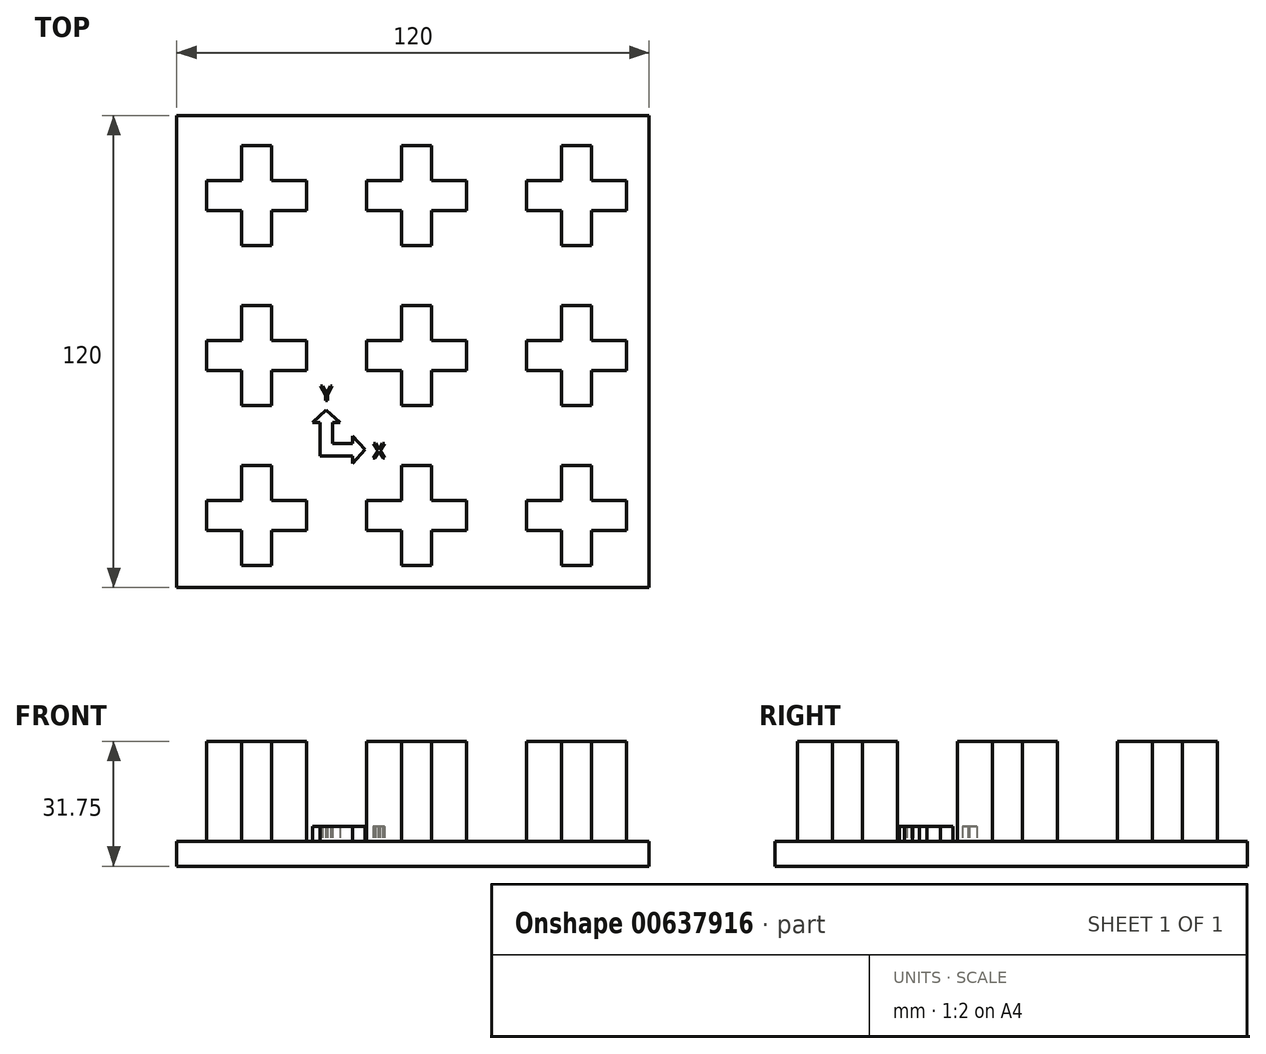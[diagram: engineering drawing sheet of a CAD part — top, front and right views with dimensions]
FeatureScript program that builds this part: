
annotation { "Feature Type Name" : "Feature", "Feature Type Description" : "" }
export const myFeature = defineFeature(function(context is Context, id is Id, definition is map)
    precondition{}
    {
        {
            var Q0;
            Q0=qCreatedBy(makeId("Top.planeOp"),FACE);
            var sketch = newSketch(context, id + "F0", { "sketchPlane" : qUnion([Q0])});
            skLineSegment(sketch, "E0.bottom", {"start": v(62.34, 71.9) * mm, "end": v(-57.66, 71.9) * mm});
            skLineSegment(sketch, "E0.top", {"start": v(62.34, -48.1) * mm, "end": v(-57.66, -48.1) * mm});
            skLineSegment(sketch, "E0.left", {"start": v(62.34, 71.9) * mm, "end": v(62.34, -48.1) * mm});
            skLineSegment(sketch, "E0.right", {"start": v(-57.66, 71.9) * mm, "end": v(-57.66, -48.1) * mm});
            skSolve(sketch);
        }
        {
            var Q0;
            Q0 = qSketchRegion(id + "F0", true);
            extrude(context, id + "F1", {"entities" : qUnion([Q0]), "depth" : 6.35 * mm, "offsetDistance" : 25.4 * mm});
        }
        {
            var Q0;
            Q0=makeQuery(id+"F1.opExtrude","CAP_FACE",FACE,{"disambiguationData":[OSD([sQuery(id+"F0.wireOp",EDGE,"E0.bottom"),sQuery(id+"F0.wireOp",EDGE,"E0.top"),sQuery(id+"F0.wireOp",EDGE,"E0.left"),sQuery(id+"F0.wireOp",EDGE,"E0.right")])],"isStart":false});
            var sketch = newSketch(context, id + "F2", { "sketchPlane" : qUnion([Q0])});
            skLineSegment(sketch, "E1.bottom", {"start": v(-41.15, 64.28) * mm, "end": v(-33.53, 64.28) * mm});
            skLineSegment(sketch, "E1.top", {"start": v(-41.15, 38.88) * mm, "end": v(-33.53, 38.88) * mm});
            skLineSegment(sketch, "E1.left", {"start": v(-41.15, 64.28) * mm, "end": v(-41.15, 38.88) * mm});
            skLineSegment(sketch, "E1.right", {"start": v(-33.53, 64.28) * mm, "end": v(-33.53, 38.88) * mm});
            skLineSegment(sketch, "E2.bottom", {"start": v(-50.04, 55.4) * mm, "end": v(-24.64, 55.4) * mm});
            skLineSegment(sketch, "E2.top", {"start": v(-50.04, 47.77) * mm, "end": v(-24.64, 47.77) * mm});
            skLineSegment(sketch, "E2.left", {"start": v(-50.04, 55.4) * mm, "end": v(-50.04, 47.77) * mm});
            skLineSegment(sketch, "E2.right", {"start": v(-24.64, 55.4) * mm, "end": v(-24.64, 47.77) * mm});
            skLineSegment(sketch, "E3.0.1.0", {"start": v(-24.64, 14.75) * mm, "end": v(-24.64, 7.13) * mm});
            skLineSegment(sketch, "E3.0.1.1", {"start": v(-41.15, 23.64) * mm, "end": v(-33.53, 23.64) * mm});
            skLineSegment(sketch, "E3.0.1.2", {"start": v(-41.15, -1.76) * mm, "end": v(-33.53, -1.76) * mm});
            skLineSegment(sketch, "E3.0.1.3", {"start": v(-41.15, 23.64) * mm, "end": v(-41.15, -1.76) * mm});
            skLineSegment(sketch, "E3.0.1.4", {"start": v(-33.53, 23.64) * mm, "end": v(-33.53, -1.76) * mm});
            skLineSegment(sketch, "E3.0.1.5", {"start": v(-50.04, 14.75) * mm, "end": v(-24.64, 14.75) * mm});
            skLineSegment(sketch, "E3.0.1.6", {"start": v(-50.04, 7.13) * mm, "end": v(-24.64, 7.13) * mm});
            skLineSegment(sketch, "E3.0.1.7", {"start": v(-50.04, 14.75) * mm, "end": v(-50.04, 7.13) * mm});
            skLineSegment(sketch, "E3.0.2.0", {"start": v(-24.64, -25.89) * mm, "end": v(-24.64, -33.5) * mm});
            skLineSegment(sketch, "E3.0.2.1", {"start": v(-41.15, -17) * mm, "end": v(-33.53, -17) * mm});
            skLineSegment(sketch, "E3.0.2.2", {"start": v(-41.15, -42.4) * mm, "end": v(-33.53, -42.4) * mm});
            skLineSegment(sketch, "E3.0.2.3", {"start": v(-41.15, -17) * mm, "end": v(-41.15, -42.4) * mm});
            skLineSegment(sketch, "E3.0.2.4", {"start": v(-33.53, -17) * mm, "end": v(-33.53, -42.4) * mm});
            skLineSegment(sketch, "E3.0.2.5", {"start": v(-50.04, -25.89) * mm, "end": v(-24.64, -25.89) * mm});
            skLineSegment(sketch, "E3.0.2.6", {"start": v(-50.04, -33.5) * mm, "end": v(-24.64, -33.5) * mm});
            skLineSegment(sketch, "E3.0.2.7", {"start": v(-50.04, -25.89) * mm, "end": v(-50.04, -33.5) * mm});
            skLineSegment(sketch, "E3.1.0.0", {"start": v(16, 55.4) * mm, "end": v(16, 47.77) * mm});
            skLineSegment(sketch, "E3.1.0.1", {"start": v(-0.5, 64.28) * mm, "end": v(7.11, 64.28) * mm});
            skLineSegment(sketch, "E3.1.0.2", {"start": v(-0.5, 38.88) * mm, "end": v(7.11, 38.88) * mm});
            skLineSegment(sketch, "E3.1.0.3", {"start": v(-0.5, 64.28) * mm, "end": v(-0.5, 38.88) * mm});
            skLineSegment(sketch, "E3.1.0.4", {"start": v(7.11, 64.28) * mm, "end": v(7.11, 38.88) * mm});
            skLineSegment(sketch, "E3.1.0.5", {"start": v(-9.4, 55.4) * mm, "end": v(16, 55.4) * mm});
            skLineSegment(sketch, "E3.1.0.6", {"start": v(-9.4, 47.77) * mm, "end": v(16, 47.77) * mm});
            skLineSegment(sketch, "E3.1.0.7", {"start": v(-9.4, 55.4) * mm, "end": v(-9.4, 47.77) * mm});
            skLineSegment(sketch, "E3.1.1.0", {"start": v(16, 14.75) * mm, "end": v(16, 7.13) * mm});
            skLineSegment(sketch, "E3.1.1.1", {"start": v(-0.5, 23.64) * mm, "end": v(7.11, 23.64) * mm});
            skLineSegment(sketch, "E3.1.1.2", {"start": v(-0.5, -1.76) * mm, "end": v(7.11, -1.76) * mm});
            skLineSegment(sketch, "E3.1.1.3", {"start": v(-0.5, 23.64) * mm, "end": v(-0.5, -1.76) * mm});
            skLineSegment(sketch, "E3.1.1.4", {"start": v(7.11, 23.64) * mm, "end": v(7.11, -1.76) * mm});
            skLineSegment(sketch, "E3.1.1.5", {"start": v(-9.4, 14.75) * mm, "end": v(16, 14.75) * mm});
            skLineSegment(sketch, "E3.1.1.6", {"start": v(-9.4, 7.13) * mm, "end": v(16, 7.13) * mm});
            skLineSegment(sketch, "E3.1.1.7", {"start": v(-9.4, 14.75) * mm, "end": v(-9.4, 7.13) * mm});
            skLineSegment(sketch, "E3.1.2.0", {"start": v(16, -25.89) * mm, "end": v(16, -33.5) * mm});
            skLineSegment(sketch, "E3.1.2.1", {"start": v(-0.5, -17) * mm, "end": v(7.11, -17) * mm});
            skLineSegment(sketch, "E3.1.2.2", {"start": v(-0.5, -42.4) * mm, "end": v(7.11, -42.4) * mm});
            skLineSegment(sketch, "E3.1.2.3", {"start": v(-0.5, -17) * mm, "end": v(-0.5, -42.4) * mm});
            skLineSegment(sketch, "E3.1.2.4", {"start": v(7.11, -17) * mm, "end": v(7.11, -42.4) * mm});
            skLineSegment(sketch, "E3.1.2.5", {"start": v(-9.4, -25.89) * mm, "end": v(16, -25.89) * mm});
            skLineSegment(sketch, "E3.1.2.6", {"start": v(-9.4, -33.5) * mm, "end": v(16, -33.5) * mm});
            skLineSegment(sketch, "E3.1.2.7", {"start": v(-9.4, -25.89) * mm, "end": v(-9.4, -33.5) * mm});
            skLineSegment(sketch, "E3.2.0.0", {"start": v(56.64, 55.4) * mm, "end": v(56.64, 47.77) * mm});
            skLineSegment(sketch, "E3.2.0.1", {"start": v(40.13, 64.28) * mm, "end": v(47.75, 64.28) * mm});
            skLineSegment(sketch, "E3.2.0.2", {"start": v(40.13, 38.88) * mm, "end": v(47.75, 38.88) * mm});
            skLineSegment(sketch, "E3.2.0.3", {"start": v(40.13, 64.28) * mm, "end": v(40.13, 38.88) * mm});
            skLineSegment(sketch, "E3.2.0.4", {"start": v(47.75, 64.28) * mm, "end": v(47.75, 38.88) * mm});
            skLineSegment(sketch, "E3.2.0.5", {"start": v(31.24, 55.4) * mm, "end": v(56.64, 55.4) * mm});
            skLineSegment(sketch, "E3.2.0.6", {"start": v(31.24, 47.77) * mm, "end": v(56.64, 47.77) * mm});
            skLineSegment(sketch, "E3.2.0.7", {"start": v(31.24, 55.4) * mm, "end": v(31.24, 47.77) * mm});
            skLineSegment(sketch, "E3.2.1.0", {"start": v(56.64, 14.75) * mm, "end": v(56.64, 7.13) * mm});
            skLineSegment(sketch, "E3.2.1.1", {"start": v(40.13, 23.64) * mm, "end": v(47.75, 23.64) * mm});
            skLineSegment(sketch, "E3.2.1.2", {"start": v(40.13, -1.76) * mm, "end": v(47.75, -1.76) * mm});
            skLineSegment(sketch, "E3.2.1.3", {"start": v(40.13, 23.64) * mm, "end": v(40.13, -1.76) * mm});
            skLineSegment(sketch, "E3.2.1.4", {"start": v(47.75, 23.64) * mm, "end": v(47.75, -1.76) * mm});
            skLineSegment(sketch, "E3.2.1.5", {"start": v(31.24, 14.75) * mm, "end": v(56.64, 14.75) * mm});
            skLineSegment(sketch, "E3.2.1.6", {"start": v(31.24, 7.13) * mm, "end": v(56.64, 7.13) * mm});
            skLineSegment(sketch, "E3.2.1.7", {"start": v(31.24, 14.75) * mm, "end": v(31.24, 7.13) * mm});
            skLineSegment(sketch, "E3.2.2.0", {"start": v(56.64, -25.89) * mm, "end": v(56.64, -33.5) * mm});
            skLineSegment(sketch, "E3.2.2.1", {"start": v(40.13, -17) * mm, "end": v(47.75, -17) * mm});
            skLineSegment(sketch, "E3.2.2.2", {"start": v(40.13, -42.4) * mm, "end": v(47.75, -42.4) * mm});
            skLineSegment(sketch, "E3.2.2.3", {"start": v(40.13, -17) * mm, "end": v(40.13, -42.4) * mm});
            skLineSegment(sketch, "E3.2.2.4", {"start": v(47.75, -17) * mm, "end": v(47.75, -42.4) * mm});
            skLineSegment(sketch, "E3.2.2.5", {"start": v(31.24, -25.89) * mm, "end": v(56.64, -25.89) * mm});
            skLineSegment(sketch, "E3.2.2.6", {"start": v(31.24, -33.5) * mm, "end": v(56.64, -33.5) * mm});
            skLineSegment(sketch, "E3.2.2.7", {"start": v(31.24, -25.89) * mm, "end": v(31.24, -33.5) * mm});
            skLineSegment(sketch, "E3.direction1", {"start": v(-41.15, 38.88) * mm, "end": v(-0.5, 38.88) * mm, "construction": true});
            skLineSegment(sketch, "E3.direction2", {"start": v(-41.15, 38.88) * mm, "end": v(-41.15, -1.76) * mm, "construction": true});
            skSolve(sketch);
        }
        {
            var Q0;
            Q0 = qSketchRegion(id + "F2", true);
            extrude(context, id + "F3", {"entities" : qUnion([Q0]), "operationType" : NewBodyOperationType.ADD, "depth" : 25.4 * mm, "offsetDistance" : 25.4 * mm});
        }
        {
            var Q0;
            Q0=makeQuery(id+"F1.opExtrude","CAP_FACE",FACE,{"disambiguationData":[OSD([sQuery(id+"F0.wireOp",EDGE,"E0.bottom"),sQuery(id+"F0.wireOp",EDGE,"E0.top"),sQuery(id+"F0.wireOp",EDGE,"E0.left"),sQuery(id+"F0.wireOp",EDGE,"E0.right")])],"isStart":false});
            var sketch = newSketch(context, id + "F4", { "sketchPlane" : qUnion([Q0])});
            skLineSegment(sketch, "E4", {"start": v(-21.26, -6.15) * mm, "end": v(-21.26, -14.63) * mm});
            skLineSegment(sketch, "E5", {"start": v(-21.26, -14.63) * mm, "end": v(-13, -14.63) * mm});
            skLineSegment(sketch, "E6", {"start": v(-18.08, -6.15) * mm, "end": v(-18.08, -11.46) * mm});
            skLineSegment(sketch, "E7", {"start": v(-18.08, -11.46) * mm, "end": v(-13, -11.46) * mm});
            skLineSegment(sketch, "E8", {"start": v(-18.08, -6.15) * mm, "end": v(-21.26, -6.15) * mm});
            skLineSegment(sketch, "E9", {"start": v(-13, -14.63) * mm, "end": v(-13, -11.46) * mm});
            skLineSegment(sketch, "E10", {"start": v(-13, -11.46) * mm, "end": v(-13, -9.55) * mm});
            skLineSegment(sketch, "E11", {"start": v(-13, -9.55) * mm, "end": v(-9.82, -13.05) * mm});
            skPoint(sketch, "E11.endSnap0", {"position": v(-13, -13.05) * mm});
            skLineSegment(sketch, "E12", {"start": v(-9.82, -13.05) * mm, "end": v(-13, -16.54) * mm});
            skLineSegment(sketch, "E13", {"start": v(-13, -16.54) * mm, "end": v(-13, -14.63) * mm});
            skLineSegment(sketch, "E14", {"start": v(-21.26, -6.15) * mm, "end": v(-23.16, -6.15) * mm});
            skLineSegment(sketch, "E15", {"start": v(-23.16, -6.15) * mm, "end": v(-19.67, -2.98) * mm});
            skPoint(sketch, "E15.endSnap0", {"position": v(-19.67, -6.15) * mm});
            skLineSegment(sketch, "E16", {"start": v(-19.67, -2.98) * mm, "end": v(-16.18, -6.15) * mm});
            skLineSegment(sketch, "E17", {"start": v(-16.18, -6.15) * mm, "end": v(-18.08, -6.15) * mm});
            skText(sketch, "E18", { "text": "Y", "fontName": "OpenSans-Regular.ttf"});
            skText(sketch, "E19", { "text": "X", "fontName": "OpenSans-Regular.ttf"});
            const initialGuessF4  = {"E18": [-0.02107, -0.00053, 1, 0, 0.00375], "E19": [-0.0078, -0.0152, 1, 0, 0.00375]};
            skSetInitialGuess(sketch, initialGuessF4);
            skSolve(sketch);
        }
        {
            var Q0;
            Q0 = qSketchRegion(id + "F4", true);
            extrude(context, id + "F5", {"entities" : qUnion([Q0]), "operationType" : NewBodyOperationType.ADD, "depth" : 3.8 * mm, "offsetDistance" : 25.4 * mm});
        }
    });
